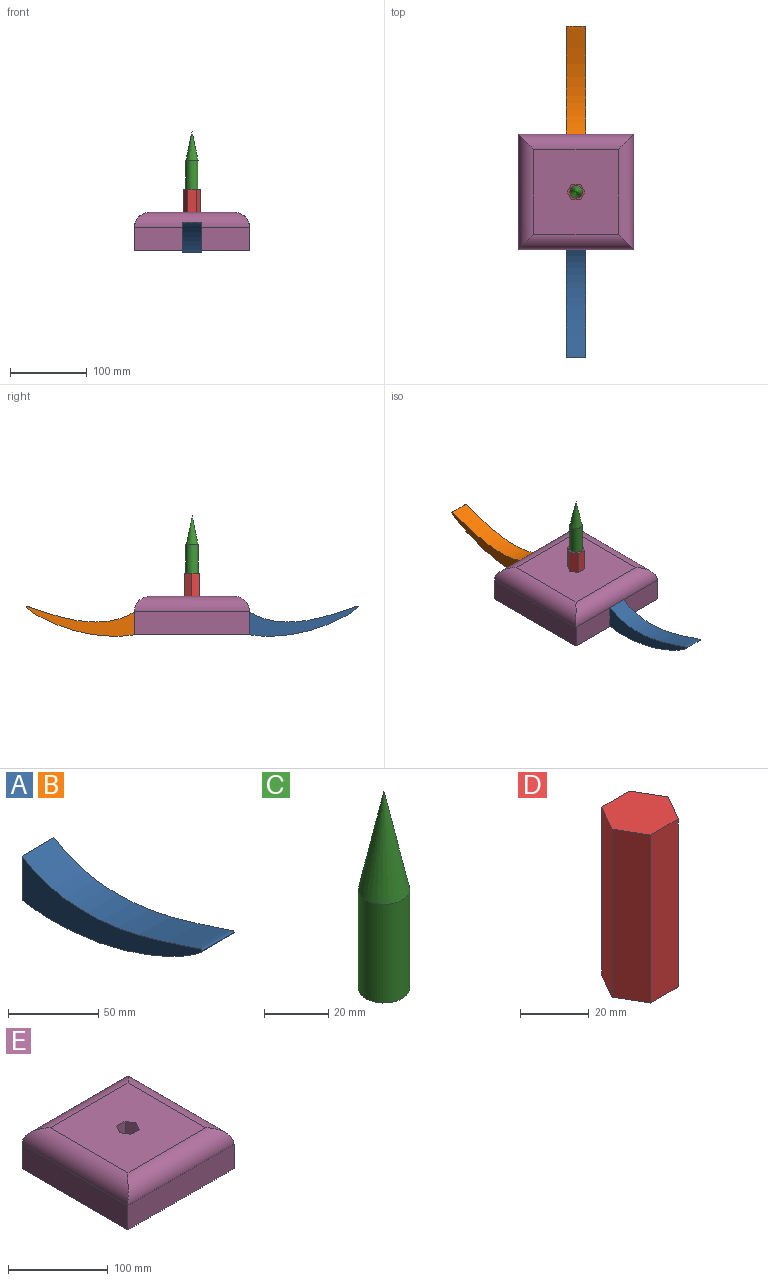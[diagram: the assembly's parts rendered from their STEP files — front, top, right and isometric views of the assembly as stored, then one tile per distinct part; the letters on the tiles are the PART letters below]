
ASSEMBLY  parts=5 mates=4
PART A: 4 faces, bbox 25x149.8x56.3 mm
  f0: plane 30x25mm, normal (0,1,0), area 750mm2, adj f1,f2,f3
  f1: extruded ~141.06x38.78mm, area 7436mm2, adj f0,f2,f3
  f2: plane 149.81x56.35mm, normal (1,0,0), area 2134.7mm2, adj f0,f1
  f3: plane 149.81x56.35mm, normal (-1,0,0), area 2134.7mm2, adj f0,f1
PART B: same geometry as A
PART C: 3 faces, bbox 16x16x75 mm
  f0: plane 16x16mm, normal (0,0,-1), area 201.1mm2, adj f1
  f1: cylinder r=8mm len=37.5mm, axis (0,0,-1), area 1885mm2, adj f0,f2
  f2: cone r=8mm half-angle=12deg, axis (0,0,-1), area 963.7mm2, adj f1
PART D: 8 faces, bbox 23.1x20x60 mm
  f0: plane 60x11.55mm, normal (0,1,0), area 692.8mm2, adj f1,f5,f6,f7
  f1: plane 60x10mm, normal (-0.87,0.5,0), area 692.8mm2, adj f0,f2,f6,f7
  f2: plane 60x10mm, normal (-0.87,-0.5,0), area 692.8mm2, adj f1,f3,f6,f7
  f3: plane 60x11.55mm, normal (0,-1,0), area 692.8mm2, adj f2,f4,f6,f7
  f4: plane 60x10mm, normal (0.87,-0.5,0), area 692.8mm2, adj f3,f5,f6,f7
  f5: plane 60x10mm, normal (0.87,0.5,0), area 692.8mm2, adj f0,f4,f6,f7
  f6: plane 23.09x20mm, normal (0,0,1), area 346.4mm2, adj f0,f1,f2,f3,f4,f5
  f7: plane 23.09x20mm, normal (0,0,-1), area 346.4mm2, adj f0,f1,f2,f3,f4,f5
PART E: 17 faces, bbox 150x150x50 mm
  f0: plane 110x110mm, normal (0,0,1), area 11753.6mm2, adj f6,f7,f8,f9,f10,f11,f13,f14
  f1: plane 150x30mm, normal (1,0,0), area 4500mm2, adj f3,f4,f5,f16
  f2: plane 150x30mm, normal (-1,0,0), area 4500mm2, adj f3,f4,f5,f13
  f3: plane 150x150mm, normal (0,0,-1), area 22500mm2, adj f1,f2,f4,f5
  f4: plane 150x30mm, normal (0,-1,0), area 4500mm2, adj f1,f2,f3,f14
  f5: plane 150x30mm, normal (0,1,0), area 4500mm2, adj f1,f2,f3,f15
  f6: plane 30x11.55mm, normal (0,-1,0), area 346.4mm2, adj f0,f7,f11,f12
  f7: plane 30x10mm, normal (0.87,-0.5,0), area 346.4mm2, adj f0,f6,f8,f12
  f8: plane 30x10mm, normal (0.87,0.5,0), area 346.4mm2, adj f0,f7,f9,f12
  f9: plane 30x11.55mm, normal (0,1,0), area 346.4mm2, adj f0,f8,f10,f12
  f10: plane 30x10mm, normal (-0.87,0.5,0), area 346.4mm2, adj f0,f9,f11,f12
  f11: plane 30x10mm, normal (-0.87,-0.5,0), area 346.4mm2, adj f0,f6,f10,f12
  f12: plane 23.09x20mm, normal (0,0,1), area 346.4mm2, adj f6,f7,f8,f9,f10,f11
  f13: cylinder r=20mm len=150mm, axis (0,1,0), area 4255.8mm2, adj f0,f2,f14,f15
  f14: cylinder r=20mm len=150mm, axis (1,0,0), area 4255.8mm2, adj f0,f4,f13,f16
  f15: cylinder r=20mm len=150mm, axis (-1,0,0), area 4255.8mm2, adj f0,f5,f13,f16
  f16: cylinder r=20mm len=150mm, axis (0,-1,0), area 4255.8mm2, adj f0,f1,f14,f15
PLACE A t=(-118.4,-79.82,138.92)mm
PLACE B rot(axis=(0,0,1),180deg) t=(-118.4,70.18,138.92)mm
PLACE C t=(-118.4,-4.82,188.92)mm
PLACE D rot(axis=(1,0,0),180deg) t=(-118.4,-4.82,158.92)mm
PLACE E t=(-118.4,-4.82,133.92)mm
MATE fastened C.f1 <-> D.f7  axis (0,0,-1) through (-118.4,-4.82,188.92)mm
MATE fastened A.f0 <-> E.f4  axis (0,1,0) through (-118.4,-79.82,123.92)mm
MATE fastened D.f6 <-> E.f12  axis (0,0,-1) through (-118.4,-4.82,128.92)mm
MATE fastened B.f0 <-> E.f5  axis (0,-1,0) through (-118.4,70.18,123.92)mm
